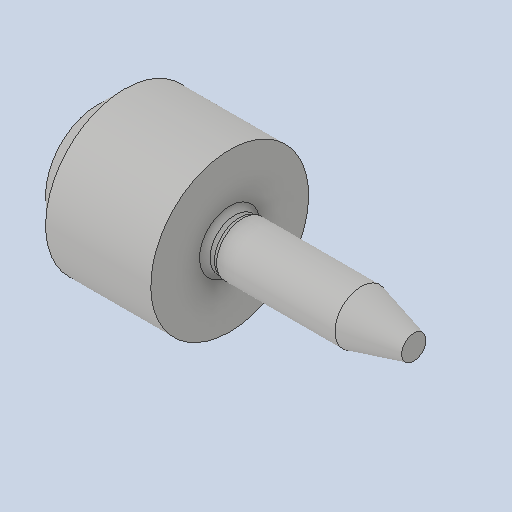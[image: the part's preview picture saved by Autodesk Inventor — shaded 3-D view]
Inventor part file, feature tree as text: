
AUTODESK INVENTOR PART (.ipt)
format: ipt  version: 2024.2 (Build 282272000, 272)  size: 145,920 bytes
history: native  units: mm
features: revolve x3, sketch x3
ambient origin geometry x8: Origin, YZ Plane, XZ Plane, XY Plane, X Axis, Y Axis, Z Axis, Center Point
bodies: Solid1 (feature_tree)
feature tree (6):
  revolve  "Revolution1"  Angle=360.0deg
  revolve  "Revolution2"  [1 undecoded]
  revolve  "Revolution3"  [1 undecoded]
  sketch  "Sketch_1"  dims[d0=360.0deg d1=360.0deg]
  sketch  "Sketch_2"  dims[d2=360.0deg]
  sketch  "Sketch_13"
note: 2 required parameter values undecoded (feature->parameter linkage not recoverable at this tier; creation-order binding heuristic only, values carry confidence <= 0.55)
